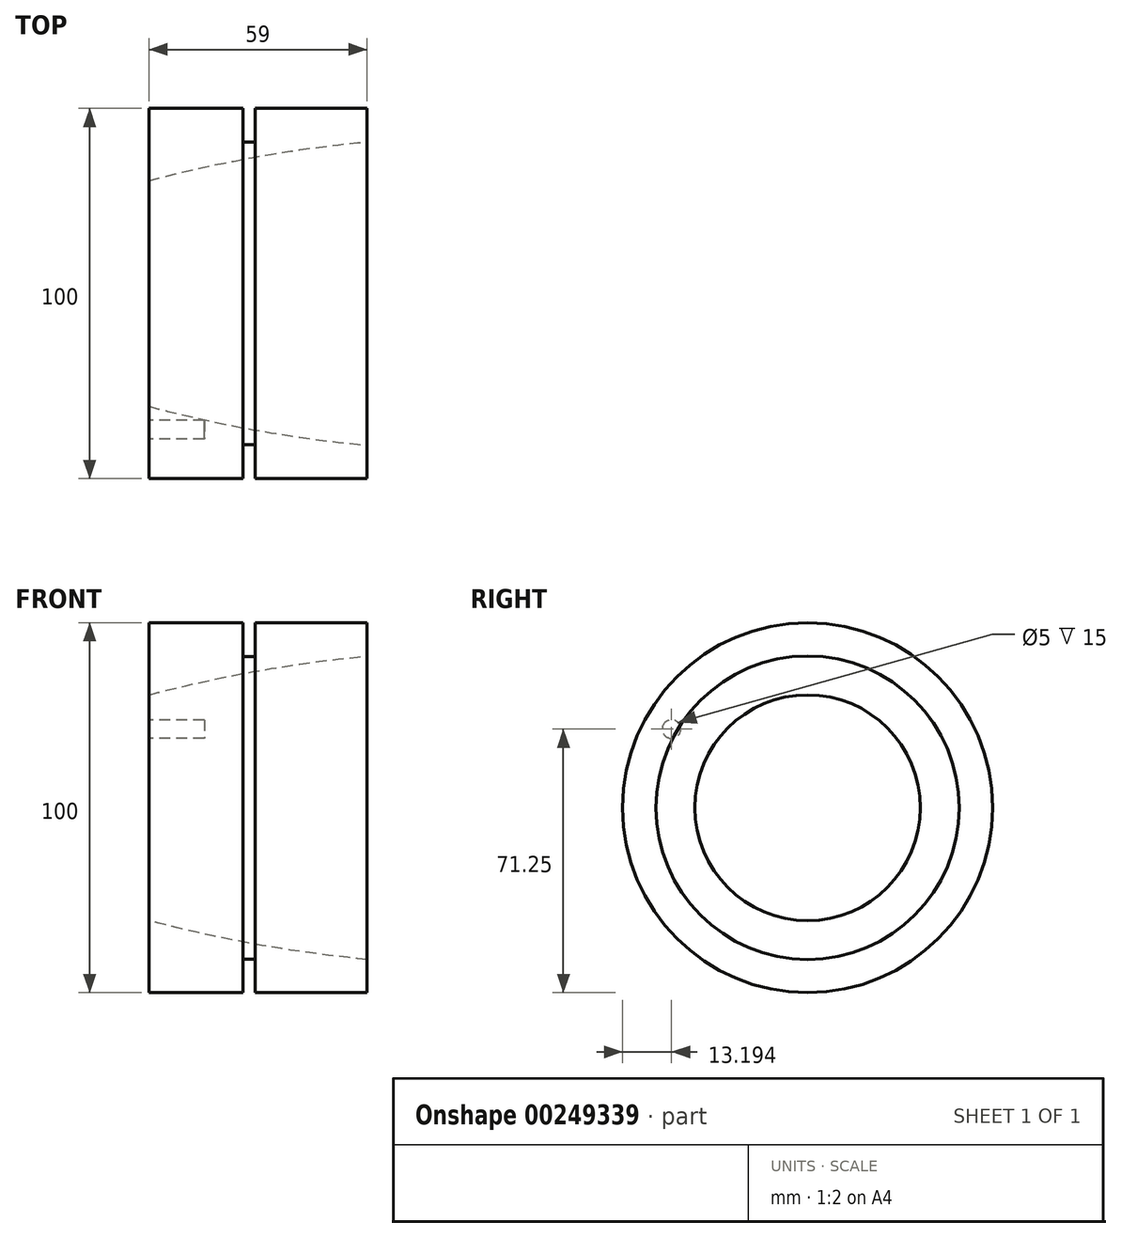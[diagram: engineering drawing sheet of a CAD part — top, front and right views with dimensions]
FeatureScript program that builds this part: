
annotation { "Feature Type Name" : "Feature", "Feature Type Description" : "" }
export const myFeature = defineFeature(function(context is Context, id is Id, definition is map)
    precondition{}
    {
        {
            var Q0;
            Q0=qCreatedBy(makeId("Front.planeOp"),FACE);
            var sketch = newSketch(context, id + "F0", { "sketchPlane" : qUnion([Q0])});
            skLineSegment(sketch, "E0", {"start": v(0, 0) * mm, "end": v(-57.54, 0) * mm, "construction": true});
            skLineSegment(sketch, "E1", {"start": v(0, 50) * mm, "end": v(0, 30.5) * mm});
            skLineSegment(sketch, "E2", {"start": v(59, 41) * mm, "end": v(59, 50) * mm});
            skLineSegment(sketch, "E3", {"start": v(0, 50) * mm, "end": v(59, 50) * mm});
            skLineSegment(sketch, "E4", {"start": v(0, 30.5) * mm, "end": v(59, 41) * mm, "construction": true});
            skArc(sketch, "E5", {"start": v(59, 41) * mm, "mid": v(29.28, 36.97) * mm, "end": v(0, 30.5) * mm});
            skLineSegment(sketch, "E6", {"start": v(29.99, 37.1) * mm, "end": v(29.99, 0) * mm, "construction": true});
            skSolve(sketch);
        }
        {
            var Q0;
            Q0=makeQuery(id+"F0.imprint","IMPRINT",FACE,{"disambiguationData":[TD([[makeQuery(id+"F0.imprint","IMPRINT",EDGE,{"derivedFrom":sQuery(id+"F0.wireOp",EDGE,"E1")}),1.0]])]});
            var Q1;
            Q1=sQuery(id+"F0.wireOp",EDGE,"E0");
            revolve(context, id + "F1", {"entities" : qUnion([Q0]), "axis" : qUnion([Q1]), "revolveType" : RevolveType.FULL});
        }
        {
            var Q0;
            Q0=makeQuery(id+"F1.opRevolve","SWEPT_FACE",FACE,{"disambiguationData":[OSD([sQuery(id+"F0.wireOp",EDGE,"E1")])]});
            var sketch = newSketch(context, id + "F2", { "sketchPlane" : qUnion([Q0])});
            skLineSegment(sketch, "E7", {"start": v(0, 0) * mm, "end": v(36.8, 21.25) * mm, "construction": true});
            skCircle(sketch, "E8", {"center": v(36.8, 21.25) * mm, "radius": 2.5 * mm});
            skSolve(sketch);
        }
        {
            var Q0;
            Q0=makeQuery(id+"F2.imprint","IMPRINT",FACE,{"disambiguationData":[TD([[makeQuery(id+"F2.imprint","IMPRINT",EDGE,{"derivedFrom":sQuery(id+"F2.wireOp",EDGE,"E8")}),1.0]])]});
            extrude(context, id + "F3", {"entities" : qUnion([Q0]), "operationType" : NewBodyOperationType.REMOVE, "oppositeDirection" : true, "depth" : 15 * mm, "offsetDistance" : 25 * mm});
        }
        {
            var Q0;
            Q0=qCreatedBy(makeId("Front.planeOp"),FACE);
            var sketch = newSketch(context, id + "F4", { "sketchPlane" : qUnion([Q0])});
            skLineSegment(sketch, "E9", {"start": v(25.5, -50) * mm, "end": v(25.5, -40.9) * mm});
            skLineSegment(sketch, "E10", {"start": v(25.5, -40.9) * mm, "end": v(28.8, -40.9) * mm});
            skLineSegment(sketch, "E11", {"start": v(28.8, -40.9) * mm, "end": v(28.8, -50) * mm});
            skLineSegment(sketch, "E12", {"start": v(0, 0) * mm, "end": v(50.58, 0) * mm, "construction": true});
            skLineSegment(sketch, "E13", {"start": v(25.5, -50) * mm, "end": v(28.8, -50) * mm});
            skSolve(sketch);
        }
        {
            var Q0;
            Q0=makeQuery(id+"F4.imprint","IMPRINT",FACE,{"disambiguationData":[TD([[makeQuery(id+"F4.imprint","IMPRINT",EDGE,{"derivedFrom":sQuery(id+"F4.wireOp",EDGE,"E9")}),-1.0]])]});
            var Q1;
            Q1=sQuery(id+"F4.wireOp",EDGE,"E12");
            revolve(context, id + "F5", {"operationType" : NewBodyOperationType.REMOVE, "entities" : qUnion([Q0]), "axis" : qUnion([Q1]), "revolveType" : RevolveType.FULL, "oppositeDirection" : true});
        }
    });
